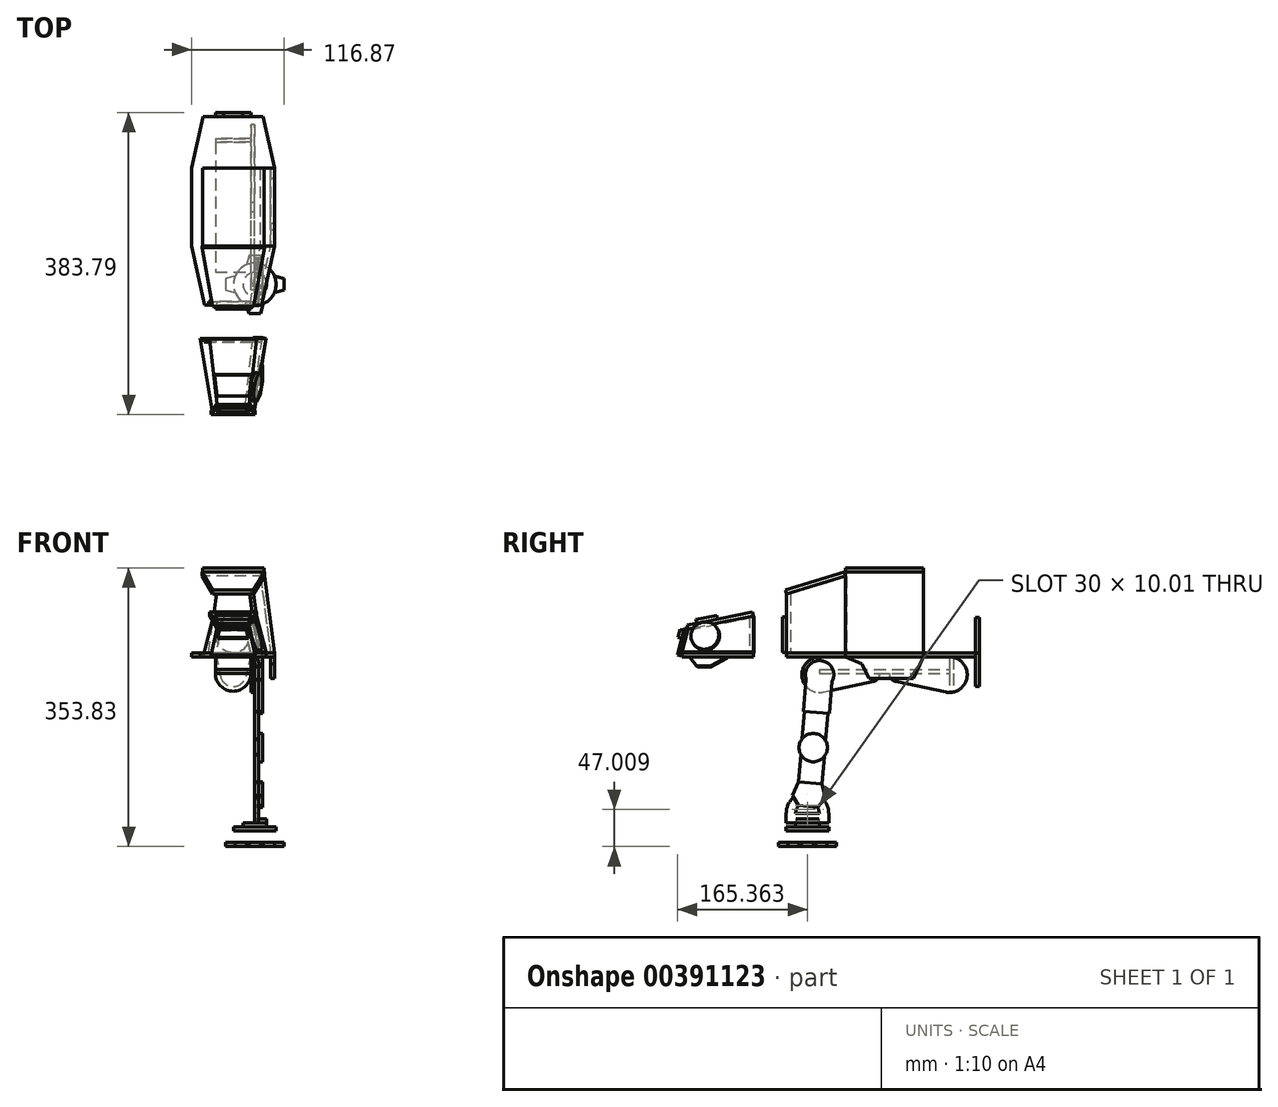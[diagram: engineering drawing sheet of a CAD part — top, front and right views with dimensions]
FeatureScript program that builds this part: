
annotation { "Feature Type Name" : "Feature", "Feature Type Description" : "" }
export const myFeature = defineFeature(function(context is Context, id is Id, definition is map)
    precondition{}
    {
        {
            assignVariable(context, id + "F0", {"name" : "unit", "anyValue" : 3});
        }
        {
            assignVariable(context, id + "F1", {"name" : "gb_thickness", "anyValue" : 5});
        }
        {
            var Q0;
            Q0=qCreatedBy(makeId("Top.planeOp"),FACE);
            var sketch = newSketch(context, id + "F2", { "sketchPlane" : qUnion([Q0])});
            skLineSegment(sketch, "E0", {"start": v(-52.5, 49.5) * mm, "end": v(-52.5, -49.5) * mm});
            skLineSegment(sketch, "E1", {"start": v(-52.5, -49.5) * mm, "end": v(-36, -124.5) * mm});
            skLineSegment(sketch, "E2", {"start": v(-36, -124.5) * mm, "end": v(36, -124.5) * mm});
            skLineSegment(sketch, "E3", {"start": v(36, -124.5) * mm, "end": v(52.5, -49.5) * mm});
            skLineSegment(sketch, "E4", {"start": v(52.5, -49.5) * mm, "end": v(52.5, 49.5) * mm});
            skLineSegment(sketch, "E5", {"start": v(52.5, 49.5) * mm, "end": v(37.98, 115.5) * mm});
            skLineSegment(sketch, "E6", {"start": v(36, 124.5) * mm, "end": v(-36, 124.5) * mm, "construction": true});
            skLineSegment(sketch, "E7", {"start": v(-36, 124.5) * mm, "end": v(-37.98, 115.5) * mm, "construction": true});
            skLineSegment(sketch, "E8", {"start": v(0, -124.5) * mm, "end": v(0, 124.5) * mm, "construction": true});
            skLineSegment(sketch, "E9", {"start": v(-52.5, 0) * mm, "end": v(52.5, 0) * mm, "construction": true});
            skLineSegment(sketch, "E10", {"start": v(37.98, 115.5) * mm, "end": v(-37.98, 115.5) * mm});
            skLineSegment(sketch, "E11", {"start": v(37.98, 115.5) * mm, "end": v(36, 124.5) * mm, "construction": true});
            skLineSegment(sketch, "E12", {"start": v(-37.98, 115.5) * mm, "end": v(-52.5, 49.5) * mm});
            skPoint(sketch, "E13", {"position": v(0, 115.5) * mm});
            skSolve(sketch);
        }
        {
            var Q0;
            Q0=qCreatedBy(makeId("Front.planeOp"),FACE);
            var sketch = newSketch(context, id + "F3", { "sketchPlane" : qUnion([Q0])});
            skLineSegment(sketch, "E14", {"start": v(-52.5, 0) * mm, "end": v(-39, 103) * mm});
            skLineSegment(sketch, "E15", {"start": v(-39, 103) * mm, "end": v(39, 103) * mm});
            skLineSegment(sketch, "E16", {"start": v(39, 103) * mm, "end": v(52.5, 0) * mm});
            skLineSegment(sketch, "E17", {"start": v(0, 0) * mm, "end": v(0, 103) * mm});
            skSolve(sketch);
        }
        {
            var Q0;
            Q0=sQuery(id+"F2.wireOp",VERTEX,"E4.start");
            var Q1;
            Q1=sQuery(id+"F2.wireOp",VERTEX,"E5.start");
            var Q2;
            Q2=sQuery(id+"F3.wireOp",VERTEX,"E16.start");
            cPlane(context, id + "F4", {"entities" : qUnion([Q0, Q1, Q2]), "cplaneType" : CPlaneType.THREE_POINT, "offset" : 25 * mm, "width" : 150 * mm, "height" : 150 * mm});
        }
        {
            var Q0;
            Q0=qCreatedBy(id+"F4.planeOp",FACE);
            var sketch = newSketch(context, id + "F5", { "sketchPlane" : qUnion([Q0])});
            skLineSegment(sketch, "E18", {"start": v(49.5, -6.82) * mm, "end": v(-49.5, -6.82) * mm});
            skLineSegment(sketch, "E19", {"start": v(-49.5, -6.82) * mm, "end": v(-49.5, 97.06) * mm});
            skLineSegment(sketch, "E20", {"start": v(-49.5, 97.06) * mm, "end": v(49.5, 97.06) * mm});
            skLineSegment(sketch, "E21", {"start": v(49.5, 97.06) * mm, "end": v(49.5, -6.82) * mm});
            skLineSegment(sketch, "E22", {"start": v(0, -6.82) * mm, "end": v(0, 97.06) * mm, "construction": true});
            skSolve(sketch);
        }
        {
            var Q0;
            Q0=sQuery(id+"F3.wireOp",VERTEX,"E15.start");
            var Q1;
            Q1=sQuery(id+"F5.wireOp",VERTEX,"E21.start");
            var Q2;
            Q2=sQuery(id+"F5.wireOp",VERTEX,"E20.start");
            cPlane(context, id + "F6", {"entities" : qUnion([Q0, Q1, Q2]), "cplaneType" : CPlaneType.THREE_POINT, "offset" : 25 * mm, "width" : 150 * mm, "height" : 150 * mm});
        }
        {
            var Q0;
            Q0=qCreatedBy(id+"F6.planeOp",FACE);
            var sketch = newSketch(context, id + "F7", { "sketchPlane" : qUnion([Q0])});
            skLineSegment(sketch, "E23", {"start": v(39, 49.5) * mm, "end": v(39, -49.5) * mm});
            skLineSegment(sketch, "E24", {"start": v(39, -49.5) * mm, "end": v(-39, -49.5) * mm});
            skLineSegment(sketch, "E25", {"start": v(-39, -49.5) * mm, "end": v(-39, 49.5) * mm});
            skLineSegment(sketch, "E26", {"start": v(-39, 49.5) * mm, "end": v(39, 49.5) * mm});
            skSolve(sketch);
        }
        {
            var Q0;
            Q0=sQuery(id+"F2.wireOp",VERTEX,"E3.start");
            var Q1;
            Q1=sQuery(id+"F5.wireOp",VERTEX,"E18.start");
            var Q2;
            Q2=sQuery(id+"F7.wireOp",VERTEX,"E23.start");
            cPlane(context, id + "F8", {"entities" : qUnion([Q0, Q1, Q2]), "cplaneType" : CPlaneType.THREE_POINT, "offset" : 25 * mm, "width" : 150 * mm, "height" : 150 * mm});
        }
        {
            var Q0;
            Q0=qCreatedBy(id+"F8.planeOp",FACE);
            var sketch = newSketch(context, id + "F9", { "sketchPlane" : qUnion([Q0])});
            skLineSegment(sketch, "E27", {"start": v(114.03, -4.68) * mm, "end": v(114.03, 71.32) * mm});
            skLineSegment(sketch, "E28", {"start": v(114.03, 71.32) * mm, "end": v(37.27, 92.06) * mm});
            skLineSegment(sketch, "E29", {"start": v(37.27, 92.06) * mm, "end": v(37.27, -6.82) * mm});
            skLineSegment(sketch, "E30", {"start": v(114.03, -4.68) * mm, "end": v(37.27, -6.82) * mm});
            skSolve(sketch);
        }
        {
            var Q0;
            Q0=sQuery(id+"F2.wireOp",VERTEX,"E2.start");
            var Q1;
            Q1=sQuery(id+"F2.wireOp",VERTEX,"E2.end");
            var Q2;
            Q2=sQuery(id+"F9.wireOp",VERTEX,"E28.start");
            cPlane(context, id + "F10", {"entities" : qUnion([Q0, Q1, Q2]), "cplaneType" : CPlaneType.THREE_POINT, "offset" : 25 * mm, "width" : 150 * mm, "height" : 150 * mm});
        }
        {
            var Q0;
            Q0=qCreatedBy(id+"F10.planeOp",FACE);
            var sketch = newSketch(context, id + "F11", { "sketchPlane" : qUnion([Q0])});
            skLineSegment(sketch, "E31", {"start": v(36, 0) * mm, "end": v(-36, 0) * mm});
            skLineSegment(sketch, "E32", {"start": v(-26.12, 75.36) * mm, "end": v(26.12, 75.36) * mm});
            skLineSegment(sketch, "E33", {"start": v(0, 0) * mm, "end": v(0, 75.36) * mm, "construction": true});
            skLineSegment(sketch, "E34", {"start": v(30.96, 0) * mm, "end": v(21.08, 75.36) * mm});
            skLineSegment(sketch, "E35", {"start": v(-21.08, 75.36) * mm, "end": v(-30.96, 0) * mm});
            skLineSegment(sketch, "E36", {"start": v(-26.12, 75.36) * mm, "end": v(-36, 0) * mm, "construction": true});
            skSolve(sketch);
        }
        {
            var Q0;
            Q0=sQuery(id+"F9.wireOp",VERTEX,"E29.start");
            var Q1;
            Q1=sQuery(id+"F9.wireOp",VERTEX,"E28.start");
            var Q2;
            Q2=sQuery(id+"F11.wireOp",VERTEX,"E32.end");
            cPlane(context, id + "F12", {"entities" : qUnion([Q0, Q1, Q2]), "cplaneType" : CPlaneType.THREE_POINT, "offset" : 25 * mm, "width" : 150 * mm, "height" : 150 * mm});
        }
        {
            var Q0;
            Q0=qCreatedBy(id+"F12.planeOp",FACE);
            var sketch = newSketch(context, id + "F13", { "sketchPlane" : qUnion([Q0])});
            skLineSegment(sketch, "E37", {"start": v(-26.12, -97.35) * mm, "end": v(26.12, -97.35) * mm});
            skLineSegment(sketch, "E38", {"start": v(26.12, -97.35) * mm, "end": v(39.65, -19) * mm});
            skLineSegment(sketch, "E39", {"start": v(39.65, -19) * mm, "end": v(-39.65, -19) * mm});
            skLineSegment(sketch, "E40", {"start": v(-26.12, -97.35) * mm, "end": v(-39.65, -19) * mm});
            skLineSegment(sketch, "E41", {"start": v(0, -19) * mm, "end": v(0, -97.35) * mm, "construction": true});
            skSolve(sketch);
        }
        {
            var Q0;
            Q0=qCreatedBy(makeId("Right.planeOp"),FACE);
            cPlane(context, id + "F14", {"entities" : qUnion([Q0]), "cplaneType" : CPlaneType.OFFSET, "offset" : ((15 * getVariable(context, 'unit')) / 2) * mm, "width" : 150 * mm, "height" : 150 * mm});
        }
        {
            var Q0;
            Q0=qCreatedBy(id+"F14.planeOp",FACE);
            var sketch = newSketch(context, id + "F15", { "sketchPlane" : qUnion([Q0])});
            skCircle(sketch, "E42", {"center": v(-82.5, -27.5) * mm, "radius": 22.5 * mm, "construction": true});
            skLineSegment(sketch, "E43", {"start": v(0, 0) * mm, "end": v(0, -26) * mm, "construction": true});
            skLineSegment(sketch, "E44", {"start": v(-82.5, -5) * mm, "end": v(82.5, -5) * mm});
            skArc(sketch, "E45", {"start": v(-82.5, -5) * mm, "mid": v(-104.88, -29.8) * mm, "end": v(-77.9, -49.53) * mm});
            skLineSegment(sketch, "E46", {"start": v(-77.9, -49.53) * mm, "end": v(-14.36, -36.28) * mm});
            skArc(sketch, "E47", {"start": v(-14.36, -36.28) * mm, "mid": v(-8.35, -32.62) * mm, "end": v(-6, -26) * mm});
            skLineSegment(sketch, "E48", {"start": v(-6, -26) * mm, "end": v(6, -26) * mm});
            skLineSegment(sketch, "E49", {"start": v(-6, -26) * mm, "end": v(-6, -5) * mm, "construction": true});
            skArc(sketch, "E50.MirrorCS", {"start": v(82.5, -5) * mm, "mid": v(104.88, -29.8) * mm, "end": v(77.9, -49.53) * mm});
            skLineSegment(sketch, "E51.MirrorCS", {"start": v(77.9, -49.53) * mm, "end": v(14.36, -36.28) * mm});
            skArc(sketch, "E52.MirrorCS", {"start": v(14.36, -36.28) * mm, "mid": v(8.35, -32.62) * mm, "end": v(6, -26) * mm});
            skSolve(sketch);
        }
        {
            var Q0;
            Q0=sQuery(id+"F15.wireOp",EDGE,"E48");
            cPoint(context, id + "F16", {"entities" : qUnion([Q0]), "parameter" : 0.5});
        }
        {
            var Q0;
            Q0 = qCreatedBy(id + "F16" ,VERTEX);
            var Q1;
            Q1=qCreatedBy(makeId("Top.planeOp"),FACE);
            cPlane(context, id + "F17", {"entities" : qUnion([Q0, Q1]), "cplaneType" : CPlaneType.PLANE_POINT, "offset" : 25 * mm, "width" : 150 * mm, "height" : 150 * mm});
        }
        {
            var Q0;
            Q0=qCreatedBy(id+"F17.planeOp",FACE);
            var sketch = newSketch(context, id + "F18", { "sketchPlane" : qUnion([Q0])});
            skLineSegment(sketch, "E53", {"start": v(22.5, -82.5) * mm, "end": v(22.5, 82.5) * mm});
            skLineSegment(sketch, "E54", {"start": v(22.5, 82.5) * mm, "end": v(-22.5, 82.5) * mm});
            skLineSegment(sketch, "E55", {"start": v(-22.5, 82.5) * mm, "end": v(-22.5, -82.5) * mm});
            skLineSegment(sketch, "E56", {"start": v(-22.5, -82.5) * mm, "end": v(22.5, -82.5) * mm});
            skLineSegment(sketch, "E57", {"start": v(0, -82.5) * mm, "end": v(0, 82.5) * mm, "construction": true});
            skSolve(sketch);
        }
        {
            var Q0;
            Q0=sQuery(id+"F18.wireOp",VERTEX,"E57.end");
            var Q1;
            Q1=qCreatedBy(makeId("Front.planeOp"),FACE);
            cPlane(context, id + "F19", {"entities" : qUnion([Q0, Q1]), "cplaneType" : CPlaneType.PLANE_POINT, "offset" : 25 * mm, "width" : 150 * mm, "height" : 150 * mm});
        }
        {
            var Q0;
            Q0=qCreatedBy(id+"F19.planeOp",FACE);
            var sketch = newSketch(context, id + "F20", { "sketchPlane" : qUnion([Q0])});
            skLineSegment(sketch, "E58", {"start": v(22.5, -5) * mm, "end": v(22.5, -26) * mm});
            skArc(sketch, "E59", {"start": v(-22.5, -26) * mm, "mid": v(0, -48.5) * mm, "end": v(22.5, -26) * mm});
            skLineSegment(sketch, "E60", {"start": v(22.5, -5) * mm, "end": v(-22.5, -5) * mm});
            skLineSegment(sketch, "E61", {"start": v(-22.5, -5) * mm, "end": v(-22.5, -26) * mm});
            skSolve(sketch);
        }
        {
            var Q0;
            Q0=sQuery(id+"F2.wireOp",EDGE,"E10");
            cPoint(context, id + "F21", {"entities" : qUnion([Q0]), "parameter" : 0.5});
        }
        {
            var Q0;
            Q0 = qCreatedBy(id + "F21" ,VERTEX);
            var Q1;
            Q1=qCreatedBy(makeId("Front.planeOp"),FACE);
            cPlane(context, id + "F22", {"entities" : qUnion([Q0, Q1]), "cplaneType" : CPlaneType.PLANE_POINT, "offset" : 25 * mm, "width" : 150 * mm, "height" : 150 * mm});
        }
        {
            var Q0;
            Q0=qCreatedBy(id+"F22.planeOp",FACE);
            var sketch = newSketch(context, id + "F23", { "sketchPlane" : qUnion([Q0])});
            skLineSegment(sketch, "E62", {"start": v(22.5, 0) * mm, "end": v(12, 45) * mm});
            skLineSegment(sketch, "E63", {"start": v(12, 45) * mm, "end": v(-12, 45) * mm});
            skLineSegment(sketch, "E64", {"start": v(-12, 45) * mm, "end": v(-22.5, 0) * mm});
            skLineSegment(sketch, "E65", {"start": v(22.5, 0) * mm, "end": v(16.13, -29.49) * mm});
            skLineSegment(sketch, "E66", {"start": v(-22.5, 0) * mm, "end": v(-16.13, -29.49) * mm});
            skArc(sketch, "E67.0", {"start": v(-22.5, -26) * mm, "mid": v(0, -48.5) * mm, "end": v(22.5, -26) * mm, "construction": true});
            skLineSegment(sketch, "E68", {"start": v(0, 0) * mm, "end": v(0, 45) * mm, "construction": true});
            skArc(sketch, "E69", {"start": v(-16.13, -29.49) * mm, "mid": v(0, -42.5) * mm, "end": v(16.13, -29.49) * mm});
            skSolve(sketch);
        }
        {
            var Q0;
            Q0=makeQuery(id+"F11.imprint","IMPRINT",FACE,{"disambiguationData":[TD([[makeQuery(id+"F11.imprint","IMPRINT",EDGE,{"derivedFrom":sQuery(id+"F11.wireOp",EDGE,"E31")}),-1.0]])]});
            var sketch = newSketch(context, id + "F24", { "sketchPlane" : qUnion([Q0])});
            skCircle(sketch, "E70", {"center": v(0, 23.5) * mm, "radius": 22.5 * mm});
            skPoint(sketch, "E71", {"position": v(0, 1) * mm});
            skSolve(sketch);
        }
        {
            var Q0;
            Q0=qCreatedBy(id+"F10.planeOp",FACE);
            cPlane(context, id + "F25", {"entities" : qUnion([Q0]), "cplaneType" : CPlaneType.OFFSET, "offset" : (14 * getVariable(context, 'unit')) * mm, "oppositeDirection" : true, "width" : 150 * mm, "height" : 150 * mm});
        }
        {
            var Q0;
            Q0=qCreatedBy(id+"F25.planeOp",FACE);
            var sketch = newSketch(context, id + "F26", { "sketchPlane" : qUnion([Q0])});
            skLineSegment(sketch, "E72", {"start": v(37, 0) * mm, "end": v(-37, 0) * mm});
            skLineSegment(sketch, "E73", {"start": v(-37, 0) * mm, "end": v(-25, 47) * mm});
            skLineSegment(sketch, "E74", {"start": v(-25, 47) * mm, "end": v(25, 47) * mm});
            skLineSegment(sketch, "E75", {"start": v(25, 47) * mm, "end": v(37, 0) * mm});
            skLineSegment(sketch, "E76", {"start": v(0, 47) * mm, "end": v(0, 0) * mm, "construction": true});
            skPoint(sketch, "E77", {"position": v(-30, 47) * mm});
            skSolve(sketch);
        }
        {
            var Q0;
            Q0=sQuery(id+"F26.wireOp",EDGE,"E72");
            cPoint(context, id + "F27", {"entities" : qUnion([Q0]), "parameter" : 0.5});
        }
        {
            var Q0;
            Q0 = qCreatedBy(id + "F27" ,VERTEX);
            var Q1;
            Q1=qCreatedBy(makeId("Top.planeOp"),FACE);
            cPlane(context, id + "F28", {"entities" : qUnion([Q0, Q1]), "cplaneType" : CPlaneType.PLANE_POINT, "offset" : 25 * mm, "width" : 150 * mm, "height" : 150 * mm});
        }
        {
            var Q0;
            Q0=qCreatedBy(id+"F28.planeOp",FACE);
            var sketch = newSketch(context, id + "F29", { "sketchPlane" : qUnion([Q0])});
            skLineSegment(sketch, "E78", {"start": v(-42, -166.5) * mm, "end": v(42, -166.5) * mm});
            skLineSegment(sketch, "E79", {"start": v(42, -166.5) * mm, "end": v(27, -257.5) * mm});
            skLineSegment(sketch, "E80", {"start": v(27, -257.5) * mm, "end": v(-27, -257.5) * mm});
            skLineSegment(sketch, "E81", {"start": v(-27, -257.5) * mm, "end": v(-42, -166.5) * mm});
            skLineSegment(sketch, "E82", {"start": v(0, -166.5) * mm, "end": v(0, -257.5) * mm, "construction": true});
            skSolve(sketch);
        }
        {
            var Q0;
            Q0=sQuery(id+"F29.wireOp",VERTEX,"E80.start");
            var Q1;
            Q1=sQuery(id+"F29.wireOp",VERTEX,"E78.end");
            var Q2;
            Q2=sQuery(id+"F26.wireOp",VERTEX,"E77");
            cPlane(context, id + "F30", {"entities" : qUnion([Q0, Q1, Q2]), "cplaneType" : CPlaneType.THREE_POINT, "offset" : 25 * mm, "width" : 150 * mm, "height" : 150 * mm});
        }
        {
            var Q0;
            Q0=qCreatedBy(id+"F30.planeOp",FACE);
            var sketch = newSketch(context, id + "F31", { "sketchPlane" : qUnion([Q0])});
            skLineSegment(sketch, "E83", {"start": v(249.83, -5.46) * mm, "end": v(242, 24.54) * mm});
            skLineSegment(sketch, "E84", {"start": v(242, 24.54) * mm, "end": v(158, 38.12) * mm});
            skLineSegment(sketch, "E85", {"start": v(158, 38.12) * mm, "end": v(158, -10.4) * mm});
            skLineSegment(sketch, "E86", {"start": v(158, -9.15) * mm, "end": v(249.83, -5.46) * mm});
            skLineSegment(sketch, "E87", {"start": v(240.15, -12.09) * mm, "end": v(231.15, -24.22) * mm});
            skLineSegment(sketch, "E88", {"start": v(231.15, -24.22) * mm, "end": v(213.17, -24.95) * mm});
            skLineSegment(sketch, "E89", {"start": v(213.17, -24.95) * mm, "end": v(192.2, -14.02) * mm});
            skLineSegment(sketch, "E90", {"start": v(192.2, -14.02) * mm, "end": v(240.15, -12.09) * mm});
            skPoint(sketch, "E91.0", {"position": v(158.76, -9.15) * mm});
            skSolve(sketch);
        }
        {
            var Q0;
            Q0=sQuery(id+"F29.wireOp",VERTEX,"E81.start");
            var Q1;
            Q1=sQuery(id+"F29.wireOp",VERTEX,"E80.start");
            var Q2;
            Q2=sQuery(id+"F31.wireOp",VERTEX,"E84.start");
            cPlane(context, id + "F32", {"entities" : qUnion([Q0, Q1, Q2]), "cplaneType" : CPlaneType.THREE_POINT, "offset" : 25 * mm, "width" : 150 * mm, "height" : 150 * mm});
        }
        {
            var Q0;
            Q0=qCreatedBy(id+"F32.planeOp",FACE);
            var sketch = newSketch(context, id + "F33", { "sketchPlane" : qUnion([Q0])});
            skLineSegment(sketch, "E92", {"start": v(-27.77, -69.34) * mm, "end": v(27.77, -69.34) * mm});
            skLineSegment(sketch, "E93", {"start": v(-27.77, -69.34) * mm, "end": v(-20.52, -33.96) * mm});
            skLineSegment(sketch, "E94", {"start": v(20.52, -33.96) * mm, "end": v(-20.52, -33.96) * mm});
            skLineSegment(sketch, "E95", {"start": v(20.52, -33.96) * mm, "end": v(27.77, -69.34) * mm});
            skLineSegment(sketch, "E96", {"start": v(0, -65.58) * mm, "end": v(0, -33.96) * mm, "construction": true});
            skSolve(sketch);
        }
        {
            var Q0;
            Q0=sQuery(id+"F33.wireOp",EDGE,"E94");
            cPoint(context, id + "F34", {"entities" : qUnion([Q0]), "parameter" : 0.5});
        }
        {
            var Q0;
            Q0 = qCreatedBy(id + "F34" ,VERTEX);
            var Q1;
            Q1=sQuery(id+"F26.wireOp",VERTEX,"E75.start");
            var Q2;
            Q2=sQuery(id+"F26.wireOp",VERTEX,"E74.start");
            cPlane(context, id + "F35", {"entities" : qUnion([Q0, Q1, Q2]), "cplaneType" : CPlaneType.THREE_POINT, "offset" : 25 * mm, "width" : 150 * mm, "height" : 150 * mm});
        }
        {
            var Q0;
            Q0=qCreatedBy(id+"F35.planeOp",FACE);
            var sketch = newSketch(context, id + "F36", { "sketchPlane" : qUnion([Q0])});
            skLineSegment(sketch, "E97", {"start": v(-20.52, -238.76) * mm, "end": v(20.52, -238.76) * mm});
            skLineSegment(sketch, "E98", {"start": v(20.52, -238.76) * mm, "end": v(30, -154.2) * mm});
            skLineSegment(sketch, "E99", {"start": v(30, -154.2) * mm, "end": v(-30, -154.2) * mm});
            skLineSegment(sketch, "E100", {"start": v(-30, -154.2) * mm, "end": v(-20.52, -238.76) * mm});
            skLineSegment(sketch, "E101", {"start": v(0, -154.2) * mm, "end": v(0, -238.76) * mm, "construction": true});
            skSolve(sketch);
        }
        {
            var Q0;
            Q0=qCreatedBy(id+"F32.planeOp",FACE);
            var sketch = newSketch(context, id + "F37", { "sketchPlane" : qUnion([Q0])});
            skLineSegment(sketch, "E102", {"start": v(17.35, -36.96) * mm, "end": v(-17.35, -36.96) * mm});
            skLineSegment(sketch, "E103", {"start": v(-19.5, -47.46) * mm, "end": v(-17.35, -36.96) * mm});
            skLineSegment(sketch, "E104", {"start": v(-19.5, -47.46) * mm, "end": v(19.5, -47.46) * mm});
            skLineSegment(sketch, "E105", {"start": v(17.35, -36.96) * mm, "end": v(19.5, -47.46) * mm});
            skLineSegment(sketch, "E106", {"start": v(0, -47.46) * mm, "end": v(0, -36.96) * mm, "construction": true});
            skPoint(sketch, "E106.startSnap0", {"position": v(0, -36.96) * mm});
            skSolve(sketch);
        }
        {
            var Q0;
            Q0=qCreatedBy(id+"F30.planeOp",FACE);
            var sketch = newSketch(context, id + "F38", { "sketchPlane" : qUnion([Q0])});
            skCircle(sketch, "E107", {"center": v(219.79, 13.86) * mm, "radius": 18 * mm});
            skLineSegment(sketch, "E108", {"start": v(244.79, 13.86) * mm, "end": v(158, 13.86) * mm, "construction": true});
            skSolve(sketch);
        }
        {
            var Q0;
            Q0=qCreatedBy(id+"F35.planeOp",FACE);
            var sketch = newSketch(context, id + "F39", { "sketchPlane" : qUnion([Q0])});
            skLineSegment(sketch, "E109", {"start": v(-20.36, -226.76) * mm, "end": v(20.36, -226.76) * mm});
            skLineSegment(sketch, "E110", {"start": v(20.36, -226.76) * mm, "end": v(23.38, -199.76) * mm});
            skLineSegment(sketch, "E111", {"start": v(23.38, -199.76) * mm, "end": v(-23.38, -199.76) * mm});
            skLineSegment(sketch, "E112", {"start": v(-23.38, -199.76) * mm, "end": v(-20.36, -226.76) * mm});
            skLineSegment(sketch, "E113", {"start": v(0, -238.76) * mm, "end": v(0, -154.2) * mm, "construction": true});
            skSolve(sketch);
        }
        {
            var Q0;
            Q0=qCreatedBy(id+"F14.planeOp",FACE);
            cPlane(context, id + "F40", {"entities" : qUnion([Q0]), "cplaneType" : CPlaneType.OFFSET, "offset" : (getVariable(context, 'gb_thickness')) * mm, "width" : 150 * mm, "height" : 150 * mm});
        }
        {
            var Q0;
            Q0=qCreatedBy(id+"F40.planeOp",FACE);
            var sketch = newSketch(context, id + "F41", { "sketchPlane" : qUnion([Q0])});
            skCircle(sketch, "E114", {"center": v(-82.5, -27.5) * mm, "radius": 18 * mm, "construction": true});
            skCircle(sketch, "E115", {"center": v(-90.6, -120.15) * mm, "radius": 18 * mm});
            skLineSegment(sketch, "E116", {"start": v(-90.6, -120.15) * mm, "end": v(-82.5, -27.5) * mm, "construction": true});
            skLineSegment(sketch, "E117", {"start": v(-99.56, -33.23) * mm, "end": v(-103.12, -73.88) * mm});
            skLineSegment(sketch, "E118", {"start": v(-103.12, -73.88) * mm, "end": v(-70.25, -76.76) * mm, "construction": true});
            skLineSegment(sketch, "E119", {"start": v(-70.25, -76.76) * mm, "end": v(-66.69, -36.1) * mm});
            skLineSegment(sketch, "E120", {"start": v(-101.63, -74.01) * mm, "end": v(-104.68, -108.93) * mm});
            skLineSegment(sketch, "E121", {"start": v(-71.74, -76.62) * mm, "end": v(-74.8, -111.54) * mm});
            skLineSegment(sketch, "E122", {"start": v(-103.12, -73.88) * mm, "end": v(-101.63, -74.01) * mm});
            skLineSegment(sketch, "E123", {"start": v(-71.74, -76.62) * mm, "end": v(-70.25, -76.76) * mm});
            skLineSegment(sketch, "E124", {"start": v(-90.6, -120.15) * mm, "end": v(-97.14, -194.86) * mm, "construction": true});
            skLineSegment(sketch, "E125", {"start": v(-109.1, -193.81) * mm, "end": v(-85.19, -195.9) * mm});
            skLineSegment(sketch, "E126", {"start": v(-85.19, -195.9) * mm, "end": v(-75.18, -184.74) * mm});
            skLineSegment(sketch, "E127", {"start": v(-75.18, -184.74) * mm, "end": v(-79.58, -166.28) * mm});
            skLineSegment(sketch, "E128", {"start": v(-79.58, -166.28) * mm, "end": v(-109.47, -163.67) * mm});
            skLineSegment(sketch, "E129", {"start": v(-109.47, -163.67) * mm, "end": v(-117.02, -181.08) * mm});
            skLineSegment(sketch, "E130", {"start": v(-117.02, -181.08) * mm, "end": v(-109.1, -193.81) * mm});
            skLineSegment(sketch, "E131", {"start": v(-109.47, -163.67) * mm, "end": v(-106.42, -128.75) * mm});
            skLineSegment(sketch, "E132", {"start": v(-79.58, -166.28) * mm, "end": v(-76.53, -131.37) * mm});
            skArc(sketch, "E133", {"start": v(-66.69, -36.1) * mm, "mid": v(-80.93, -9.57) * mm, "end": v(-99.56, -33.23) * mm});
            skArc(sketch, "E134", {"start": v(-104.68, -108.93) * mm, "mid": v(-108.54, -118.58) * mm, "end": v(-106.42, -128.75) * mm});
            skArc(sketch, "E135", {"start": v(-76.53, -131.37) * mm, "mid": v(-72.67, -121.71) * mm, "end": v(-74.8, -111.54) * mm});
            skCircle(sketch, "E136", {"center": v(-97.93, -203.83) * mm, "radius": 15 * mm, "construction": true});
            skCircle(sketch, "E137", {"center": v(-97.93, -203.83) * mm, "radius": 27 * mm, "construction": true});
            skArc(sketch, "E138", {"start": v(-109.1, -193.81) * mm, "mid": v(-111.94, -198.47) * mm, "end": v(-112.93, -203.83) * mm});
            skArc(sketch, "E139", {"start": v(-82.93, -203.83) * mm, "mid": v(-83.5, -199.7) * mm, "end": v(-85.19, -195.9) * mm});
            skArc(sketch, "E140", {"start": v(-70.93, -203.83) * mm, "mid": v(-72.49, -194.77) * mm, "end": v(-77, -186.77) * mm});
            skArc(sketch, "E141", {"start": v(-115.58, -183.4) * mm, "mid": v(-122.48, -192.6) * mm, "end": v(-124.93, -203.83) * mm});
            skLineSegment(sketch, "E142", {"start": v(-82.93, -203.83) * mm, "end": v(-82.93, -203.83) * mm});
            skLineSegment(sketch, "E143", {"start": v(-82.93, -203.83) * mm, "end": v(-112.93, -203.83) * mm});
            skLineSegment(sketch, "E144", {"start": v(-97.93, -203.83) * mm, "end": v(-97.93, -203.83) * mm});
            skLineSegment(sketch, "E145", {"start": v(-70.93, -203.83) * mm, "end": v(-70.93, -215.83) * mm});
            skLineSegment(sketch, "E146", {"start": v(-70.93, -215.83) * mm, "end": v(-124.93, -215.83) * mm});
            skLineSegment(sketch, "E147.MirrorCS", {"start": v(-124.93, -203.83) * mm, "end": v(-124.93, -215.83) * mm});
            skPoint(sketch, "E148", {"position": v(-97.93, -215.83) * mm});
            skLineSegment(sketch, "E149", {"start": v(-97.93, -215.83) * mm, "end": v(-97.93, -203.83) * mm, "construction": true});
            skSolve(sketch);
        }
        {
            var Q0;
            Q0=sQuery(id+"F41.wireOp",EDGE,"E149");
            var Q1;
            Q1=sQuery(id+"F41.wireOp",VERTEX,"E148");
            cPlane(context, id + "F42", {"entities" : qUnion([Q0, Q1]), "cplaneType" : CPlaneType.LINE_POINT, "offset" : 25 * mm, "width" : 150 * mm, "height" : 150 * mm});
        }
        {
            var Q0;
            Q0=qCreatedBy(id+"F42.planeOp",FACE);
            var sketch = newSketch(context, id + "F43", { "sketchPlane" : qUnion([Q0])});
            skCircle(sketch, "E150", {"center": v(27.5, -97.93) * mm, "radius": 15 * mm});
            skLineSegment(sketch, "E151", {"start": v(30, -112.72) * mm, "end": v(30, -83.14) * mm});
            skLineSegment(sketch, "E152", {"start": v(25, -112.72) * mm, "end": v(25, -83.14) * mm});
            skLineSegment(sketch, "E153", {"start": v(27.5, -112.93) * mm, "end": v(27.5, -82.93) * mm, "construction": true});
            skSolve(sketch);
        }
        {
            var Q0;
            Q0=qCreatedBy(id+"F42.planeOp",FACE);
            cPlane(context, id + "F44", {"entities" : qUnion([Q0]), "cplaneType" : CPlaneType.OFFSET, "offset" : (1 * getVariable(context, 'gb_thickness')) * mm, "oppositeDirection" : true, "width" : 150 * mm, "height" : 150 * mm});
        }
        {
            var Q0;
            Q0=qCreatedBy(id+"F44.planeOp",FACE);
            var sketch = newSketch(context, id + "F45", { "sketchPlane" : qUnion([Q0])});
            skCircle(sketch, "E154", {"center": v(27.5, -97.93) * mm, "radius": 27 * mm});
            skLineSegment(sketch, "E155", {"start": v(52.37, -108.43) * mm, "end": v(64.37, -105.43) * mm});
            skLineSegment(sketch, "E156", {"start": v(64.37, -105.43) * mm, "end": v(64.37, -90.43) * mm});
            skLineSegment(sketch, "E157", {"start": v(64.37, -90.43) * mm, "end": v(52.37, -87.43) * mm});
            skLineSegment(sketch, "E158", {"start": v(27.5, -97.93) * mm, "end": v(64.37, -97.93) * mm, "construction": true});
            skLineSegment(sketch, "E159.1.0", {"start": v(20, -61.05) * mm, "end": v(17, -73.05) * mm});
            skLineSegment(sketch, "E159.1.1", {"start": v(35, -61.05) * mm, "end": v(20, -61.05) * mm});
            skLineSegment(sketch, "E159.1.2", {"start": v(38, -73.05) * mm, "end": v(35, -61.05) * mm});
            skLineSegment(sketch, "E159.2.0", {"start": v(-9.37, -105.43) * mm, "end": v(2.63, -108.43) * mm});
            skLineSegment(sketch, "E159.2.1", {"start": v(-9.37, -90.43) * mm, "end": v(-9.37, -105.43) * mm});
            skLineSegment(sketch, "E159.2.2", {"start": v(2.63, -87.43) * mm, "end": v(-9.37, -90.43) * mm});
            skLineSegment(sketch, "E159.3.0", {"start": v(35, -134.8) * mm, "end": v(38, -122.8) * mm});
            skLineSegment(sketch, "E159.3.1", {"start": v(20, -134.8) * mm, "end": v(35, -134.8) * mm});
            skLineSegment(sketch, "E159.3.2", {"start": v(17, -122.8) * mm, "end": v(20, -134.8) * mm});
            skSolve(sketch);
        }
        {
            var Q0;
            Q0=sQuery(id+"F2.wireOp",VERTEX,"E9.end");
            var Q1;
            Q1=qCreatedBy(makeId("Right.planeOp"),FACE);
            cPlane(context, id + "F46", {"entities" : qUnion([Q0, Q1]), "cplaneType" : CPlaneType.PLANE_POINT, "offset" : 25 * mm, "width" : 150 * mm, "height" : 150 * mm});
        }
        {
            var Q0;
            Q0=qCreatedBy(id+"F46.planeOp",FACE);
            var sketch = newSketch(context, id + "F47", { "sketchPlane" : qUnion([Q0])});
            skLineSegment(sketch, "E160", {"start": v(-49.5, -5) * mm, "end": v(-28.5, -14) * mm});
            skLineSegment(sketch, "E161", {"start": v(-28.5, -14) * mm, "end": v(-20.1, -32) * mm});
            skLineSegment(sketch, "E162", {"start": v(-20.1, -32) * mm, "end": v(36.9, -32) * mm});
            skLineSegment(sketch, "E163", {"start": v(36.9, -32) * mm, "end": v(49.5, -5) * mm});
            skLineSegment(sketch, "E164", {"start": v(49.5, -5) * mm, "end": v(-49.5, -5) * mm});
            skLineSegment(sketch, "E165", {"start": v(8.4, -32) * mm, "end": v(8.4, -5) * mm, "construction": true});
            skSolve(sketch);
        }
        {
            var Q0;
            Q0=makeQuery(id+"F2.imprint","IMPRINT",FACE,{"disambiguationData":[TD([[makeQuery(id+"F2.imprint","IMPRINT",EDGE,{"derivedFrom":sQuery(id+"F2.wireOp",EDGE,"E0")}),1.0]])]});
            extrude(context, id + "F48", {"entities" : qUnion([Q0]), "oppositeDirection" : true, "depth" : (getVariable(context, 'gb_thickness')) * mm});
        }
        {
            var Q0;
            Q0=makeQuery(id+"F5.imprint","IMPRINT",FACE,{"disambiguationData":[TD([[makeQuery(id+"F5.imprint","IMPRINT",EDGE,{"derivedFrom":sQuery(id+"F5.wireOp",EDGE,"E18")}),-1.0]])]});
            extrude(context, id + "F49", {"entities" : qUnion([Q0]), "depth" : (getVariable(context, 'gb_thickness')) * mm});
        }
        {
            var Q0;
            Q0=makeQuery(id+"F7.imprint","IMPRINT",FACE,{"disambiguationData":[TD([[makeQuery(id+"F7.imprint","IMPRINT",EDGE,{"derivedFrom":sQuery(id+"F7.wireOp",EDGE,"E23")}),-1.0]])]});
            extrude(context, id + "F50", {"entities" : qUnion([Q0]), "oppositeDirection" : true, "depth" : (getVariable(context, 'gb_thickness')) * mm});
        }
        {
            var Q0;
            Q0=makeQuery(id+"F9.imprint","IMPRINT",FACE,{"disambiguationData":[TD([[makeQuery(id+"F9.imprint","IMPRINT",EDGE,{"derivedFrom":sQuery(id+"F9.wireOp",EDGE,"E27")}),1.0]])]});
            extrude(context, id + "F51", {"entities" : qUnion([Q0]), "depth" : (getVariable(context, 'gb_thickness')) * mm});
        }
        {
            var Q0;
            Q0=makeQuery(id+"F13.imprint","IMPRINT",FACE,{"disambiguationData":[TD([[makeQuery(id+"F13.imprint","IMPRINT",EDGE,{"derivedFrom":sQuery(id+"F13.wireOp",EDGE,"E37")}),1.0]])]});
            extrude(context, id + "F52", {"entities" : qUnion([Q0]), "depth" : (getVariable(context, 'gb_thickness')) * mm});
        }
        {
            var Q0;
            Q0=makeQuery(id+"F24.imprint","IMPRINT",FACE,{"disambiguationData":[TD([[makeQuery(id+"F24.imprint","IMPRINT",EDGE,{"derivedFrom":sQuery(id+"F24.wireOp",EDGE,"E70")}),1.0]])]});
            var Q1;
            Q1=makeQuery(id+"F24.imprint","IMPRINT",FACE,{"disambiguationData":[TD([[makeQuery(id+"F24.imprint","IMPRINT",EDGE,{"derivedFrom":sQuery(id+"F24.wireOp",EDGE,"E70")}),-1.0]])]});
            extrude(context, id + "F53", {"entities" : qUnion([Q0, Q1]), "depth" : (getVariable(context, 'gb_thickness')) * mm});
        }
        {
            var Q0;
            Q0=makeQuery(id+"F15.imprint","IMPRINT",FACE,{"disambiguationData":[TD([[makeQuery(id+"F15.imprint","IMPRINT",EDGE,{"derivedFrom":sQuery(id+"F15.wireOp",EDGE,"E44")}),-1.0]])]});
            extrude(context, id + "F54", {"entities" : qUnion([Q0]), "depth" : (getVariable(context, 'gb_thickness')) * mm});
        }
        {
            var Q0;
            Q0=makeQuery(id+"F18.imprint","IMPRINT",FACE,{"disambiguationData":[TD([[makeQuery(id+"F18.imprint","IMPRINT",EDGE,{"derivedFrom":sQuery(id+"F18.wireOp",EDGE,"E53")}),1.0]])]});
            extrude(context, id + "F55", {"entities" : qUnion([Q0]), "depth" : (getVariable(context, 'gb_thickness')) * mm});
        }
        {
            var Q0;
            Q0 = qSketchRegion(id + "F20", true);
            extrude(context, id + "F56", {"entities" : qUnion([Q0]), "oppositeDirection" : true, "depth" : (getVariable(context, 'gb_thickness')) * mm});
        }
        {
            var Q0;
            Q0=makeQuery(id+"F23.imprint","IMPRINT",FACE,{"disambiguationData":[TD([[makeQuery(id+"F23.imprint","IMPRINT",EDGE,{"derivedFrom":sQuery(id+"F23.wireOp",EDGE,"E62")}),1.0]])]});
            extrude(context, id + "F57", {"entities" : qUnion([Q0]), "oppositeDirection" : true, "depth" : (getVariable(context, 'gb_thickness')) * mm});
        }
        {
            var Q0;
            Q0=makeQuery(id+"F24.imprint","IMPRINT",FACE,{"disambiguationData":[TD([[makeQuery(id+"F24.imprint","IMPRINT",EDGE,{"derivedFrom":sQuery(id+"F24.wireOp",EDGE,"E70")}),1.0]])]});
            extrude(context, id + "F58", {"entities" : qUnion([Q0]), "oppositeDirection" : true, "depth" : 5 * mm});
        }
        {
            var Q0;
            Q0=makeQuery(id+"F47.imprint","IMPRINT",FACE,{"disambiguationData":[TD([[makeQuery(id+"F47.imprint","IMPRINT",EDGE,{"derivedFrom":sQuery(id+"F47.wireOp",EDGE,"E160")}),1.0]])]});
            extrude(context, id + "F59", {"entities" : qUnion([Q0]), "oppositeDirection" : true, "depth" : (getVariable(context, 'gb_thickness')) * mm});
        }
        {
            var Q0;
            Q0=makeQuery(id+"F29.imprint","IMPRINT",FACE,{"disambiguationData":[TD([[makeQuery(id+"F29.imprint","IMPRINT",EDGE,{"derivedFrom":sQuery(id+"F29.wireOp",EDGE,"E78")}),-1.0]])]});
            extrude(context, id + "F60", {"entities" : qUnion([Q0]), "oppositeDirection" : true, "depth" : (getVariable(context, 'gb_thickness')) * mm});
        }
        {
            var Q0;
            Q0=makeQuery(id+"F26.imprint","IMPRINT",FACE,{"disambiguationData":[TD([[makeQuery(id+"F26.imprint","IMPRINT",EDGE,{"derivedFrom":sQuery(id+"F26.wireOp",EDGE,"E72")}),-1.0]])]});
            extrude(context, id + "F61", {"entities" : qUnion([Q0]), "oppositeDirection" : true, "depth" : (getVariable(context, 'gb_thickness')) * mm});
        }
        {
            var Q0;
            Q0=makeQuery(id+"F31.imprint","IMPRINT",FACE,{"disambiguationData":[TD([[makeQuery(id+"F31.imprint","IMPRINT",EDGE,{"derivedFrom":sQuery(id+"F31.wireOp",EDGE,"E83")}),1.0]])]});
            extrude(context, id + "F62", {"entities" : qUnion([Q0]), "depth" : (getVariable(context, 'gb_thickness')) * mm});
        }
        {
            var Q0;
            Q0=makeQuery(id+"F36.imprint","IMPRINT",FACE,{"disambiguationData":[TD([[makeQuery(id+"F36.imprint","IMPRINT",EDGE,{"derivedFrom":sQuery(id+"F36.wireOp",EDGE,"E97")}),1.0]])]});
            extrude(context, id + "F63", {"entities" : qUnion([Q0]), "depth" : (getVariable(context, 'gb_thickness')) * mm});
        }
        {
            var Q0;
            Q0=makeQuery(id+"F33.imprint","IMPRINT",FACE,{"disambiguationData":[TD([[makeQuery(id+"F33.imprint","IMPRINT",EDGE,{"derivedFrom":sQuery(id+"F33.wireOp",EDGE,"E92")}),1.0]])]});
            extrude(context, id + "F64", {"entities" : qUnion([Q0]), "oppositeDirection" : true, "depth" : (getVariable(context, 'gb_thickness')) * mm});
        }
        {
            var Q0;
            Q0=makeQuery(id+"F37.imprint","IMPRINT",FACE,{"disambiguationData":[TD([[makeQuery(id+"F37.imprint","IMPRINT",EDGE,{"derivedFrom":sQuery(id+"F37.wireOp",EDGE,"E102")}),1.0]])]});
            extrude(context, id + "F65", {"entities" : qUnion([Q0]), "oppositeDirection" : true, "depth" : (2 * getVariable(context, 'gb_thickness')) * mm, "hasSecondDirection" : true, "secondDirectionOppositeDirection" : true, "secondDirectionDepth" : (getVariable(context, 'gb_thickness')) * mm});
        }
        {
            var Q0;
            Q0=makeQuery(id+"F39.imprint","IMPRINT",FACE,{"disambiguationData":[TD([[makeQuery(id+"F39.imprint","IMPRINT",EDGE,{"derivedFrom":sQuery(id+"F39.wireOp",EDGE,"E109")}),1.0]])]});
            extrude(context, id + "F66", {"entities" : qUnion([Q0]), "depth" : (2 * getVariable(context, 'gb_thickness')) * mm, "hasSecondDirection" : true, "secondDirectionOppositeDirection" : false, "secondDirectionDepth" : (getVariable(context, 'gb_thickness')) * mm});
        }
        {
            var Q0;
            Q0=makeQuery(id+"F38.imprint","IMPRINT",FACE,{"disambiguationData":[TD([[makeQuery(id+"F38.imprint","IMPRINT",EDGE,{"derivedFrom":sQuery(id+"F38.wireOp",EDGE,"E107")}),1.0]])]});
            extrude(context, id + "F67", {"entities" : qUnion([Q0]), "oppositeDirection" : true, "depth" : (getVariable(context, 'gb_thickness')) * mm});
        }
        {
            var Q0;
            Q0=makeQuery(id+"F41.imprint","IMPRINT",FACE,{"disambiguationData":[TD([[makeQuery(id+"F41.imprint","IMPRINT",EDGE,{"derivedFrom":sQuery(id+"F41.wireOp",EDGE,"E117")}),1.0]])]});
            var Q1;
            {var subQ0=sQuery(id+"F41.wireOp",EDGE,"E115");var subQ1=makeQuery(id+"F41.imprint","INTERSECT",VERTEX,{"derivedFrom":[subQ0,sQuery(id+"F41.wireOp",EDGE,"E120")]});Q1=makeQuery(id+"F41.imprint","IMPRINT",FACE,{"disambiguationData":[TD([[makeQuery(id+"F41.imprint","IMPRINT",EDGE,{"disambiguationData":[TD([[subQ1,1.0]])],"derivedFrom":subQ0}),1.0]])]});}
            var Q2;
            Q2=makeQuery(id+"F41.imprint","IMPRINT",FACE,{"disambiguationData":[TD([[makeQuery(id+"F41.imprint","IMPRINT",EDGE,{"derivedFrom":sQuery(id+"F41.wireOp",EDGE,"E128")}),-1.0]])]});
            var Q3;
            {var subQ3=sQuery(id+"F41.wireOp",EDGE,"E125");Q3=makeQuery(id+"F41.imprint","IMPRINT",FACE,{"disambiguationData":[TD([[makeQuery(id+"F41.imprint","IMPRINT",EDGE,{"derivedFrom":subQ3}),1.0]])]});}
            var Q4;
            {var subQ4=sQuery(id+"F41.wireOp",EDGE,"E138");Q4=makeQuery(id+"F41.imprint","IMPRINT",FACE,{"disambiguationData":[TD([[makeQuery(id+"F41.imprint","IMPRINT",EDGE,{"derivedFrom":subQ4}),-1.0]])]});}
            extrude(context, id + "F68", {"entities" : qUnion([Q0, Q1, Q2, Q3, Q4]), "depth" : (getVariable(context, 'gb_thickness')) * mm});
        }
        {
            var Q0;
            {var subQ0=sQuery(id+"F41.wireOp",EDGE,"E115");var subQ1=makeQuery(id+"F41.imprint","INTERSECT",VERTEX,{"derivedFrom":[subQ0,sQuery(id+"F41.wireOp",EDGE,"E120")]});Q0=makeQuery(id+"F41.imprint","IMPRINT",FACE,{"disambiguationData":[TD([[makeQuery(id+"F41.imprint","IMPRINT",EDGE,{"disambiguationData":[TD([[subQ1,1.0]])],"derivedFrom":subQ0}),1.0]])]});}
            extrude(context, id + "F69", {"entities" : qUnion([Q0]), "depth" : (2 * getVariable(context, 'gb_thickness')) * mm, "hasSecondDirection" : true, "secondDirectionOppositeDirection" : false, "secondDirectionDepth" : (getVariable(context, 'gb_thickness')) * mm});
        }
        {
            var Q0;
            {var subQ0=sQuery(id+"F43.wireOp",EDGE,"E151");Q0=makeQuery(id+"F43.imprint","IMPRINT",FACE,{"disambiguationData":[TD([[makeQuery(id+"F43.imprint","IMPRINT",EDGE,{"derivedFrom":subQ0}),-1.0]])]});}
            extrude(context, id + "F70", {"entities" : qUnion([Q0]), "depth" : (getVariable(context, 'gb_thickness')) * mm});
        }
        {
            var Q0;
            {var subQ0=sQuery(id+"F43.wireOp",EDGE,"E152");Q0=makeQuery(id+"F43.imprint","IMPRINT",FACE,{"disambiguationData":[TD([[makeQuery(id+"F43.imprint","IMPRINT",EDGE,{"derivedFrom":subQ0}),1.0]])]});}
            var Q1;
            {var subQ0=sQuery(id+"F43.wireOp",EDGE,"E151");Q1=makeQuery(id+"F43.imprint","IMPRINT",FACE,{"disambiguationData":[TD([[makeQuery(id+"F43.imprint","IMPRINT",EDGE,{"derivedFrom":subQ0}),1.0]])]});}
            var Q2;
            {var subQ0=sQuery(id+"F43.wireOp",EDGE,"E151");Q2=makeQuery(id+"F43.imprint","IMPRINT",FACE,{"disambiguationData":[TD([[makeQuery(id+"F43.imprint","IMPRINT",EDGE,{"derivedFrom":subQ0}),-1.0]])]});}
            extrude(context, id + "F71", {"entities" : qUnion([Q0, Q1, Q2]), "oppositeDirection" : true, "depth" : (getVariable(context, 'gb_thickness')) * mm});
        }
        {
            var Q0;
            {var subQ0=sQuery(id+"F45.wireOp",EDGE,"E154");var subQ5=makeQuery(id+"F45.imprint","INTERSECT",VERTEX,{"derivedFrom":[subQ0,sQuery(id+"F45.wireOp",EDGE,"E157")]});Q0=makeQuery(id+"F45.imprint","IMPRINT",FACE,{"disambiguationData":[TD([[makeQuery(id+"F45.imprint","IMPRINT",EDGE,{"disambiguationData":[TD([[subQ5,-1.0]])],"derivedFrom":subQ0}),1.0]])]});}
            extrude(context, id + "F72", {"entities" : qUnion([Q0]), "oppositeDirection" : true, "depth" : (getVariable(context, 'gb_thickness')) * mm});
        }
        {
            var Q0;
            {var subQ0=sQuery(id+"F45.wireOp",EDGE,"E159.3.0");Q0=makeQuery(id+"F45.imprint","IMPRINT",FACE,{"disambiguationData":[TD([[makeQuery(id+"F45.imprint","IMPRINT",EDGE,{"derivedFrom":subQ0}),1.0]])]});}
            var Q1;
            {var subQ0=sQuery(id+"F45.wireOp",EDGE,"E154");var subQ5=makeQuery(id+"F45.imprint","INTERSECT",VERTEX,{"derivedFrom":[subQ0,sQuery(id+"F45.wireOp",EDGE,"E157")]});Q1=makeQuery(id+"F45.imprint","IMPRINT",FACE,{"disambiguationData":[TD([[makeQuery(id+"F45.imprint","IMPRINT",EDGE,{"disambiguationData":[TD([[subQ5,-1.0]])],"derivedFrom":subQ0}),1.0]])]});}
            var Q2;
            {var subQ0=sQuery(id+"F45.wireOp",EDGE,"E159.2.0");Q2=makeQuery(id+"F45.imprint","IMPRINT",FACE,{"disambiguationData":[TD([[makeQuery(id+"F45.imprint","IMPRINT",EDGE,{"derivedFrom":subQ0}),1.0]])]});}
            var Q3;
            {var subQ0=sQuery(id+"F45.wireOp",EDGE,"E159.1.0");Q3=makeQuery(id+"F45.imprint","IMPRINT",FACE,{"disambiguationData":[TD([[makeQuery(id+"F45.imprint","IMPRINT",EDGE,{"derivedFrom":subQ0}),1.0]])]});}
            var Q4;
            {var subQ0=sQuery(id+"F45.wireOp",EDGE,"E155");Q4=makeQuery(id+"F45.imprint","IMPRINT",FACE,{"disambiguationData":[TD([[makeQuery(id+"F45.imprint","IMPRINT",EDGE,{"derivedFrom":subQ0}),1.0]])]});}
            extrude(context, id + "F73", {"entities" : qUnion([Q0, Q1, Q2, Q3, Q4]), "oppositeDirection" : true, "depth" : (5 * getVariable(context, 'gb_thickness')) * mm, "hasSecondDirection" : true, "secondDirectionOppositeDirection" : true, "secondDirectionDepth" : (4 * getVariable(context, 'gb_thickness')) * mm});
        }
        {
            var Q0;
            Q0=makeQuery(id+"F31.imprint","IMPRINT",FACE,{"disambiguationData":[TD([[makeQuery(id+"F31.imprint","IMPRINT",EDGE,{"derivedFrom":sQuery(id+"F31.wireOp",EDGE,"E87")}),-1.0]])]});
            extrude(context, id + "F74", {"entities" : qUnion([Q0]), "depth" : (getVariable(context, 'gb_thickness')) * mm});
        }
        {
            var Q0;
            Q0=makeQuery(id+"F68.opExtrude","CAP_FACE",FACE,{"disambiguationData":[OSD([sQuery(id+"F41.wireOp",EDGE,"E115"),sQuery(id+"F41.wireOp",EDGE,"E117"),sQuery(id+"F41.wireOp",EDGE,"E119"),sQuery(id+"F41.wireOp",EDGE,"E120"),sQuery(id+"F41.wireOp",EDGE,"E121"),sQuery(id+"F41.wireOp",EDGE,"E122"),sQuery(id+"F41.wireOp",EDGE,"E123"),sQuery(id+"F41.wireOp",EDGE,"E125"),sQuery(id+"F41.wireOp",EDGE,"E126"),sQuery(id+"F41.wireOp",EDGE,"E127"),sQuery(id+"F41.wireOp",EDGE,"E129"),sQuery(id+"F41.wireOp",EDGE,"E130"),sQuery(id+"F41.wireOp",EDGE,"E131"),sQuery(id+"F41.wireOp",EDGE,"E132"),sQuery(id+"F41.wireOp",EDGE,"E133"),sQuery(id+"F41.wireOp",EDGE,"E138"),sQuery(id+"F41.wireOp",EDGE,"E139"),sQuery(id+"F41.wireOp",EDGE,"E140"),sQuery(id+"F41.wireOp",EDGE,"E141"),sQuery(id+"F41.wireOp",EDGE,"E143"),sQuery(id+"F41.wireOp",EDGE,"E145"),sQuery(id+"F41.wireOp",EDGE,"E146"),sQuery(id+"F41.wireOp",EDGE,"E147.MirrorCS")])],"isStart":false});
            var sketch = newSketch(context, id + "F75", { "sketchPlane" : qUnion([Q0])});
            skLineSegment(sketch, "E166.0", {"start": v(-79.58, -166.28) * mm, "end": v(-109.47, -163.67) * mm});
            skLineSegment(sketch, "E166.1", {"start": v(-109.47, -163.67) * mm, "end": v(-117.02, -181.08) * mm});
            skLineSegment(sketch, "E166.2", {"start": v(-117.02, -181.08) * mm, "end": v(-109.1, -193.81) * mm});
            skLineSegment(sketch, "E166.3", {"start": v(-109.1, -193.81) * mm, "end": v(-85.19, -195.9) * mm});
            skLineSegment(sketch, "E166.4", {"start": v(-85.19, -195.9) * mm, "end": v(-75.18, -184.74) * mm});
            skLineSegment(sketch, "E166.5", {"start": v(-75.18, -184.74) * mm, "end": v(-79.58, -166.28) * mm});
            skSolve(sketch);
        }
        {
            var Q0;
            Q0=makeQuery(id+"F75.imprint","IMPRINT",FACE,{"disambiguationData":[TD([[makeQuery(id+"F75.imprint","IMPRINT",EDGE,{"derivedFrom":sQuery(id+"F75.wireOp",EDGE,"E166.0")}),1.0]])]});
            extrude(context, id + "F76", {"entities" : qUnion([Q0]), "depth" : (getVariable(context, 'gb_thickness')) * mm});
        }
        {
            var Q0;
            Q0=makeQuery(id+"F68.opExtrude","CAP_FACE",FACE,{"disambiguationData":[OSD([sQuery(id+"F41.wireOp",EDGE,"E115"),sQuery(id+"F41.wireOp",EDGE,"E117"),sQuery(id+"F41.wireOp",EDGE,"E119"),sQuery(id+"F41.wireOp",EDGE,"E120"),sQuery(id+"F41.wireOp",EDGE,"E121"),sQuery(id+"F41.wireOp",EDGE,"E122"),sQuery(id+"F41.wireOp",EDGE,"E123"),sQuery(id+"F41.wireOp",EDGE,"E125"),sQuery(id+"F41.wireOp",EDGE,"E126"),sQuery(id+"F41.wireOp",EDGE,"E127"),sQuery(id+"F41.wireOp",EDGE,"E129"),sQuery(id+"F41.wireOp",EDGE,"E130"),sQuery(id+"F41.wireOp",EDGE,"E131"),sQuery(id+"F41.wireOp",EDGE,"E132"),sQuery(id+"F41.wireOp",EDGE,"E133"),sQuery(id+"F41.wireOp",EDGE,"E138"),sQuery(id+"F41.wireOp",EDGE,"E139"),sQuery(id+"F41.wireOp",EDGE,"E140"),sQuery(id+"F41.wireOp",EDGE,"E141"),sQuery(id+"F41.wireOp",EDGE,"E143"),sQuery(id+"F41.wireOp",EDGE,"E145"),sQuery(id+"F41.wireOp",EDGE,"E146"),sQuery(id+"F41.wireOp",EDGE,"E147.MirrorCS")])],"isStart":false});
            var sketch = newSketch(context, id + "F77", { "sketchPlane" : qUnion([Q0])});
            skLineSegment(sketch, "E167.0", {"start": v(-103.12, -73.88) * mm, "end": v(-70.25, -76.76) * mm});
            skLineSegment(sketch, "E167.1", {"start": v(-70.25, -76.76) * mm, "end": v(-66.69, -36.1) * mm});
            skLineSegment(sketch, "E167.2", {"start": v(-99.56, -33.23) * mm, "end": v(-103.12, -73.88) * mm});
            skArc(sketch, "E167.3", {"start": v(-66.69, -36.1) * mm, "mid": v(-80.93, -9.57) * mm, "end": v(-99.56, -33.23) * mm});
            skSolve(sketch);
        }
        {
            var Q0;
            Q0 = qSketchRegion(id + "F77", true);
            extrude(context, id + "F78", {"entities" : qUnion([Q0]), "depth" : (getVariable(context, 'gb_thickness')) * mm});
        }
    });
